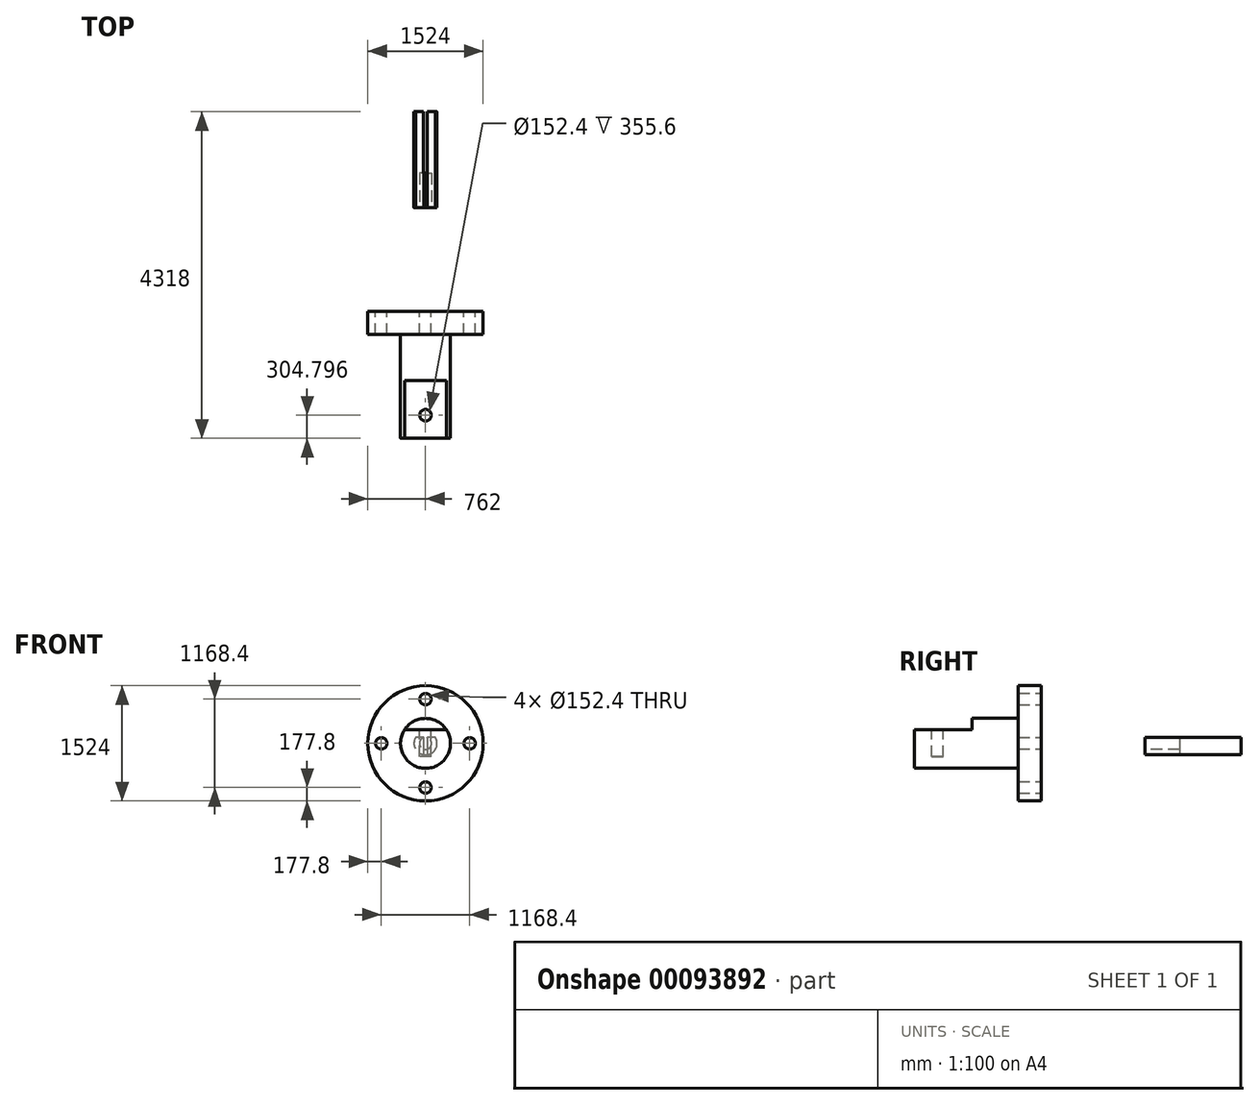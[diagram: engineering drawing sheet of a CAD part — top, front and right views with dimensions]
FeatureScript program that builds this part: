
annotation { "Feature Type Name" : "Feature", "Feature Type Description" : "" }
export const myFeature = defineFeature(function(context is Context, id is Id, definition is map)
    precondition{}
    {
        {
            var Q0;
            Q0=qCreatedBy(makeId("Right.planeOp"),FACE);
            var sketch = newSketch(context, id + "F0", { "sketchPlane" : qUnion([Q0])});
            skLineSegment(sketch, "E0", {"start": v(-809.36, 0) * mm, "end": v(3508.64, 0) * mm});
            skLineSegment(sketch, "E1", {"start": v(-809.36, 0) * mm, "end": v(-809.36, 330.2) * mm});
            skLineSegment(sketch, "E2", {"start": v(-809.36, 330.2) * mm, "end": v(562.24, 330.2) * mm});
            skLineSegment(sketch, "E3", {"start": v(562.24, 330.2) * mm, "end": v(562.24, 0) * mm});
            skLineSegment(sketch, "E4", {"start": v(562.24, 0) * mm, "end": v(562.24, 330.2) * mm});
            skLineSegment(sketch, "E5", {"start": v(562.24, 0) * mm, "end": v(562.24, 762) * mm});
            skLineSegment(sketch, "E6", {"start": v(562.24, 762) * mm, "end": v(867.04, 762) * mm});
            skLineSegment(sketch, "E7", {"start": v(867.04, 762) * mm, "end": v(867.04, 0) * mm});
            skLineSegment(sketch, "E8", {"start": v(867.04, 0) * mm, "end": v(867.04, 330.2) * mm});
            skLineSegment(sketch, "E9", {"start": v(867.04, 330.2) * mm, "end": v(1197.24, 330.2) * mm});
            skLineSegment(sketch, "E10", {"start": v(1197.24, 330.2) * mm, "end": v(1197.24, 0) * mm});
            skLineSegment(sketch, "E11", {"start": v(1197.24, 0) * mm, "end": v(1197.24, 279.4) * mm});
            skLineSegment(sketch, "E12", {"start": v(1197.24, 279.4) * mm, "end": v(1425.84, 279.4) * mm});
            skLineSegment(sketch, "E13", {"start": v(1425.84, 279.4) * mm, "end": v(1425.84, 0) * mm});
            skLineSegment(sketch, "E14", {"start": v(1425.84, 0) * mm, "end": v(1425.84, 279.4) * mm});
            skLineSegment(sketch, "E15", {"start": v(1425.84, 279.4) * mm, "end": v(1425.84, 330.2) * mm});
            skLineSegment(sketch, "E16", {"start": v(1425.84, 330.2) * mm, "end": v(1629.04, 330.2) * mm});
            skLineSegment(sketch, "E17", {"start": v(1629.04, 330.2) * mm, "end": v(1629.04, 0) * mm});
            skLineSegment(sketch, "E18", {"start": v(1629.04, 0) * mm, "end": v(1629.04, 330.2) * mm});
            skLineSegment(sketch, "E19", {"start": v(1629.04, 330.2) * mm, "end": v(2010.04, 228.6) * mm});
            skLineSegment(sketch, "E20", {"start": v(2010.04, 228.6) * mm, "end": v(2010.04, 0) * mm});
            skLineSegment(sketch, "E21", {"start": v(2010.04, 0) * mm, "end": v(2010.04, 152.4) * mm});
            skLineSegment(sketch, "E22", {"start": v(2010.04, 152.4) * mm, "end": v(3508.64, 152.4) * mm});
            skLineSegment(sketch, "E23", {"start": v(3508.64, 152.4) * mm, "end": v(3508.64, 0) * mm});
            skLineSegment(sketch, "E24", {"start": v(2238.64, 152.4) * mm, "end": v(2238.64, 79.66) * mm});
            skLineSegment(sketch, "E25", {"start": v(2238.64, 79.66) * mm, "end": v(3508.64, 79.66) * mm});
            skLineSegment(sketch, "E26", {"start": v(2695.84, 152.4) * mm, "end": v(2695.84, 0) * mm});
            skSolve(sketch);
        }
        {
            var Q0;
            {var subQ0=sQuery(id+"F0.wireOp",EDGE,"E1");Q0=makeQuery(id+"F0.imprint","IMPRINT",FACE,{"disambiguationData":[TD([[makeQuery(id+"F0.imprint","IMPRINT",EDGE,{"derivedFrom":subQ0}),-1.0]])]});}
            var Q1;
            {var subQ0=sQuery(id+"F0.wireOp",EDGE,"E6");Q1=makeQuery(id+"F0.imprint","IMPRINT",FACE,{"disambiguationData":[TD([[makeQuery(id+"F0.imprint","IMPRINT",EDGE,{"derivedFrom":subQ0}),-1.0]])]});}
            var Q2;
            {var subQ0=sQuery(id+"F0.wireOp",EDGE,"E8");Q2=makeQuery(id+"F0.imprint","IMPRINT",FACE,{"disambiguationData":[TD([[makeQuery(id+"F0.imprint","IMPRINT",EDGE,{"derivedFrom":subQ0}),-1.0]])]});}
            var Q3;
            {var subQ0=sQuery(id+"F0.wireOp",EDGE,"E11");Q3=makeQuery(id+"F0.imprint","IMPRINT",FACE,{"disambiguationData":[TD([[makeQuery(id+"F0.imprint","IMPRINT",EDGE,{"derivedFrom":subQ0}),-1.0]])]});}
            var Q4;
            {var subQ0=sQuery(id+"F0.wireOp",EDGE,"E14");Q4=makeQuery(id+"F0.imprint","IMPRINT",FACE,{"disambiguationData":[TD([[makeQuery(id+"F0.imprint","IMPRINT",EDGE,{"derivedFrom":subQ0}),-1.0]])]});}
            var Q5;
            {var subQ0=sQuery(id+"F0.wireOp",EDGE,"E18");Q5=makeQuery(id+"F0.imprint","IMPRINT",FACE,{"disambiguationData":[TD([[makeQuery(id+"F0.imprint","IMPRINT",EDGE,{"derivedFrom":subQ0}),-1.0]])]});}
            var Q6;
            {var subQ1=sQuery(id+"F0.wireOp",EDGE,"E21");Q6=makeQuery(id+"F0.imprint","IMPRINT",FACE,{"disambiguationData":[TD([[makeQuery(id+"F0.imprint","IMPRINT",EDGE,{"derivedFrom":subQ1}),-1.0]])]});}
            var Q7;
            {var subQ0=sQuery(id+"F0.wireOp",EDGE,"E23");var subQ1=sQuery(id+"F0.wireOp",EDGE,"E0");var subQ2=makeQuery(id+"F0.imprint","INTERSECT",VERTEX,{"derivedFrom":[subQ1,subQ0]});Q7=makeQuery(id+"F0.imprint","IMPRINT",FACE,{"disambiguationData":[TD([[makeQuery(id+"F0.imprint","IMPRINT",EDGE,{"disambiguationData":[TD([[subQ2,1.0]])],"derivedFrom":subQ1}),1.0]])]});}
            var Q8;
            {var subQ0=sQuery(id+"F0.wireOp",EDGE,"E23");var subQ1=sQuery(id+"F0.wireOp",EDGE,"E22");var subQ2=makeQuery(id+"F0.imprint","INTERSECT",VERTEX,{"derivedFrom":[subQ1,subQ0]});Q8=makeQuery(id+"F0.imprint","IMPRINT",FACE,{"disambiguationData":[TD([[makeQuery(id+"F0.imprint","IMPRINT",EDGE,{"disambiguationData":[TD([[subQ2,1.0]])],"derivedFrom":subQ1}),-1.0]])]});}
            var Q9;
            {var subQ0=sQuery(id+"F0.wireOp",EDGE,"E24");Q9=makeQuery(id+"F0.imprint","IMPRINT",FACE,{"disambiguationData":[TD([[makeQuery(id+"F0.imprint","IMPRINT",EDGE,{"derivedFrom":subQ0}),1.0]])]});}
            var Q10;
            Q10=sQuery(id+"F0.wireOp",EDGE,"E0");
            revolve(context, id + "F1", {"entities" : qUnion([Q0, Q1, Q2, Q3, Q4, Q5, Q6, Q7, Q8, Q9]), "axis" : qUnion([Q10]), "revolveType" : RevolveType.FULL});
        }
        {
            var Q0;
            Q0=makeQuery(id+"F1.opRevolve","SWEPT_FACE",FACE,{"disambiguationData":[OSD([sQuery(id+"F0.wireOp",EDGE,"E7")])]});
            var sketch = newSketch(context, id + "F2", { "sketchPlane" : qUnion([Q0])});
            skCircle(sketch, "E27", {"center": v(0, 584.2) * mm, "radius": 76.2 * mm});
            skCircle(sketch, "E28", {"center": v(584.2, 0) * mm, "radius": 76.2 * mm});
            skCircle(sketch, "E29", {"center": v(0, -584.2) * mm, "radius": 76.2 * mm});
            skCircle(sketch, "E30", {"center": v(-584.2, 0) * mm, "radius": 76.2 * mm});
            skSolve(sketch);
        }
        {
            var Q0;
            Q0=makeQuery(id+"F2.imprint","IMPRINT",FACE,{"disambiguationData":[TD([[makeQuery(id+"F2.imprint","IMPRINT",EDGE,{"derivedFrom":sQuery(id+"F2.wireOp",EDGE,"E30")}),1.0]])]});
            var Q1;
            Q1=makeQuery(id+"F2.imprint","IMPRINT",FACE,{"disambiguationData":[TD([[makeQuery(id+"F2.imprint","IMPRINT",EDGE,{"derivedFrom":sQuery(id+"F2.wireOp",EDGE,"E27")}),1.0]])]});
            var Q2;
            Q2=makeQuery(id+"F2.imprint","IMPRINT",FACE,{"disambiguationData":[TD([[makeQuery(id+"F2.imprint","IMPRINT",EDGE,{"derivedFrom":sQuery(id+"F2.wireOp",EDGE,"E29")}),1.0]])]});
            var Q3;
            Q3=makeQuery(id+"F2.imprint","IMPRINT",FACE,{"disambiguationData":[TD([[makeQuery(id+"F2.imprint","IMPRINT",EDGE,{"derivedFrom":sQuery(id+"F2.wireOp",EDGE,"E28")}),1.0]])]});
            extrude(context, id + "F3", {"entities" : qUnion([Q0, Q1, Q2, Q3]), "operationType" : NewBodyOperationType.REMOVE, "endBound" : BoundingType.THROUGH_ALL, "oppositeDirection" : true, "depth" : 25.4 * mm});
        }
        {
            var Q0;
            Q0=makeQuery(id+"F1.opRevolve","SWEPT_FACE",FACE,{"disambiguationData":[OSD([sQuery(id+"F0.wireOp",EDGE,"E1")])]});
            var sketch = newSketch(context, id + "F4", { "sketchPlane" : qUnion([Q0])});
            skLineSegment(sketch, "E31", {"start": v(-278.24, 177.8) * mm, "end": v(278.24, 177.8) * mm});
            skSolve(sketch);
        }
        {
            var Q0;
            {var subQ0=sQuery(id+"F4.wireOp",EDGE,"E31");Q0=makeQuery(id+"F4.imprint","IMPRINT",FACE,{"disambiguationData":[TD([[makeQuery(id+"F4.imprint","IMPRINT",EDGE,{"derivedFrom":subQ0}),1.0]])]});}
            extrude(context, id + "F5", {"entities" : qUnion([Q0]), "operationType" : NewBodyOperationType.REMOVE, "oppositeDirection" : true, "depth" : 762 * mm});
        }
        {
            var Q0;
            Q0=makeQuery(id+"F5.boolean.opBoolean","COPY",FACE,{"derivedFrom":makeQuery(id+"F5.opExtrude","SWEPT_FACE",FACE,{"disambiguationData":[OSD([sQuery(id+"F4.wireOp",EDGE,"E31")])]})});
            var sketch = newSketch(context, id + "F6", { "sketchPlane" : qUnion([Q0])});
            skCircle(sketch, "E32", {"center": v(0, -504.56) * mm, "radius": 76.2 * mm});
            skPoint(sketch, "E32.centerSnap0", {"position": v(0, -809.36) * mm});
            skSolve(sketch);
        }
        {
            var Q0;
            Q0=makeQuery(id+"F6.imprint","IMPRINT",FACE,{"disambiguationData":[TD([[makeQuery(id+"F6.imprint","IMPRINT",EDGE,{"derivedFrom":sQuery(id+"F6.wireOp",EDGE,"E32")}),1.0]])]});
            extrude(context, id + "F7", {"entities" : qUnion([Q0]), "operationType" : NewBodyOperationType.REMOVE, "oppositeDirection" : true, "depth" : 355.6 * mm});
        }
        {
            var Q0;
            Q0=makeQuery(id+"F1.opRevolve","SWEPT_FACE",FACE,{"disambiguationData":[OSD([sQuery(id+"F0.wireOp",EDGE,"E23")])]});
            var sketch = newSketch(context, id + "F8", { "sketchPlane" : qUnion([Q0])});
            skLineSegment(sketch, "E33", {"start": v(-131.98, 76.2) * mm, "end": v(131.98, 76.2) * mm});
            skSolve(sketch);
        }
        {
            var Q0;
            {var subQ0=sQuery(id+"F8.wireOp",EDGE,"E33");Q0=makeQuery(id+"F8.imprint","IMPRINT",FACE,{"disambiguationData":[TD([[makeQuery(id+"F8.imprint","IMPRINT",EDGE,{"derivedFrom":subQ0}),1.0]])]});}
            extrude(context, id + "F9", {"entities" : qUnion([Q0]), "operationType" : NewBodyOperationType.REMOVE, "oppositeDirection" : true, "depth" : 1270 * mm});
        }
        {
            var Q0;
            Q0=makeQuery(id+"F1.opRevolve","SWEPT_FACE",FACE,{"disambiguationData":[OSD([sQuery(id+"F0.wireOp",EDGE,"E23")])]});
            var sketch = newSketch(context, id + "F10", { "sketchPlane" : qUnion([Q0])});
            skLineSegment(sketch, "E34", {"start": v(0, 76.2) * mm, "end": v(0, -152.4) * mm, "construction": true});
            skLineSegment(sketch, "E35", {"start": v(-25.4, 76.2) * mm, "end": v(-25.4, -150.27) * mm});
            skLineSegment(sketch, "E36.MirrorCS", {"start": v(25.4, 76.2) * mm, "end": v(25.4, -150.27) * mm});
            skSolve(sketch);
        }
        {
            var Q0;
            {var subQ0=sQuery(id+"F10.wireOp",EDGE,"E35");Q0=makeQuery(id+"F10.imprint","IMPRINT",FACE,{"disambiguationData":[TD([[makeQuery(id+"F10.imprint","IMPRINT",EDGE,{"derivedFrom":subQ0}),1.0]])]});}
            extrude(context, id + "F11", {"entities" : qUnion([Q0]), "operationType" : NewBodyOperationType.REMOVE, "oppositeDirection" : true, "depth" : 812.8 * mm});
        }
    });
